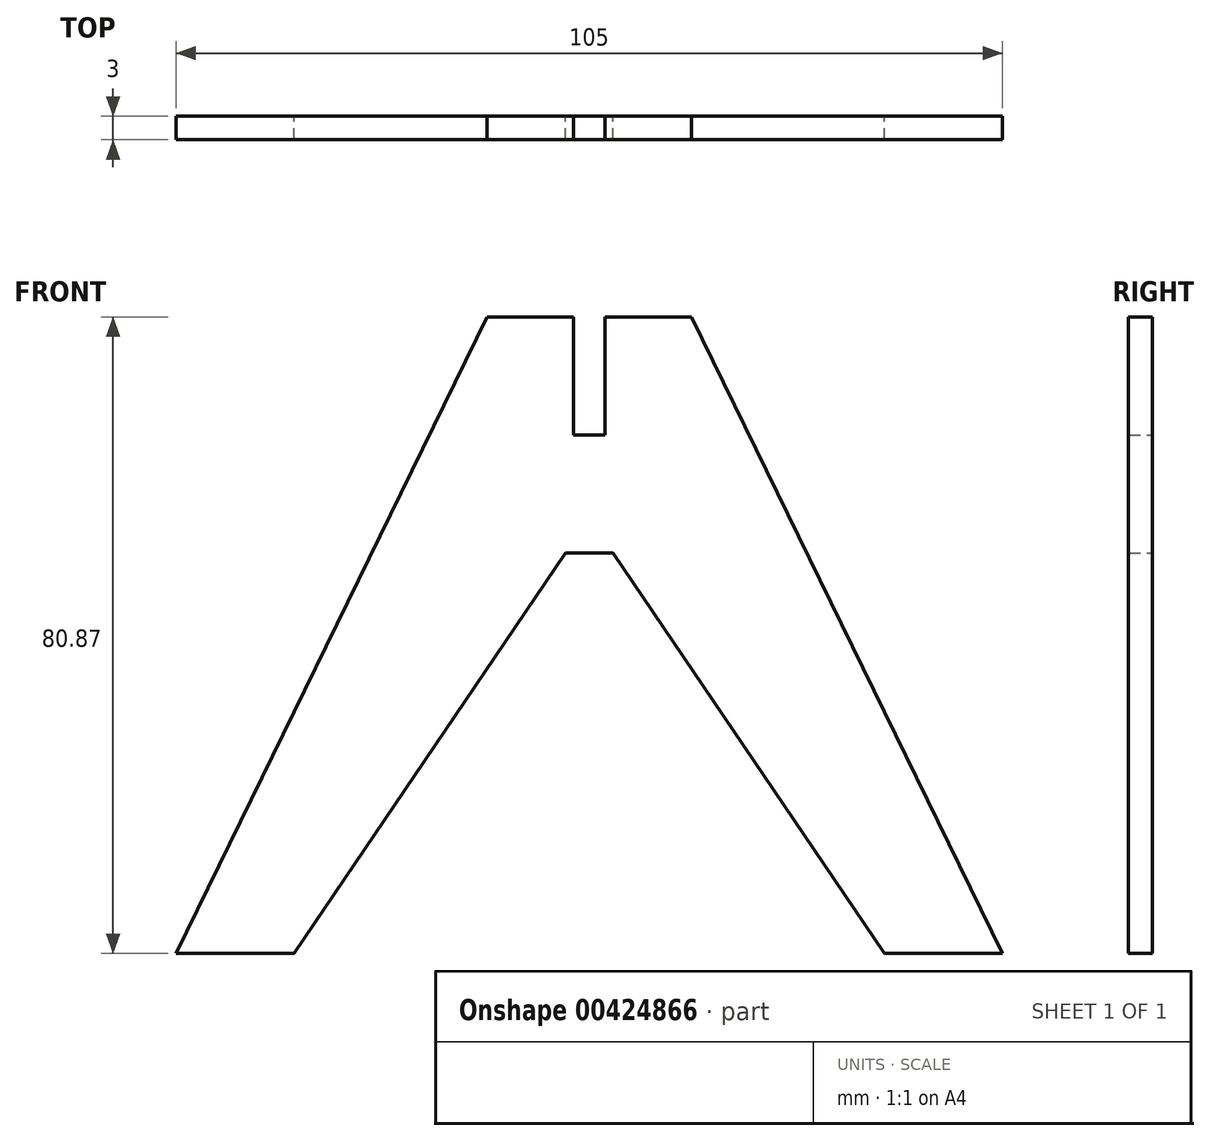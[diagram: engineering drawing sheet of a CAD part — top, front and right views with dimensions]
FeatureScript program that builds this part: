
annotation { "Feature Type Name" : "Feature", "Feature Type Description" : "" }
export const myFeature = defineFeature(function(context is Context, id is Id, definition is map)
    precondition{}
    {
        {
            var Q0;
            Q0=qCreatedBy(makeId("Front.planeOp"),FACE);
            var sketch = newSketch(context, id + "F0", { "sketchPlane" : qUnion([Q0])});
            skLineSegment(sketch, "E0", {"start": v(-77.39, -80.87) * mm, "end": v(-62.39, -80.87) * mm});
            skLineSegment(sketch, "E1", {"start": v(27.61, -80.87) * mm, "end": v(12.61, -80.87) * mm});
            skLineSegment(sketch, "E2", {"start": v(-37.89, 0) * mm, "end": v(-77.39, -80.87) * mm});
            skLineSegment(sketch, "E3", {"start": v(-11.89, 0) * mm, "end": v(27.61, -80.87) * mm});
            skPoint(sketch, "E4.orphan", {"position": v(-24.89, -80.87) * mm});
            skPoint(sketch, "E5.orphan", {"position": v(-24.89, -40.43) * mm});
            skLineSegment(sketch, "E6", {"start": v(-24.89, -30) * mm, "end": v(-27.89, -30) * mm});
            skLineSegment(sketch, "E7", {"start": v(-24.89, -30) * mm, "end": v(-21.89, -30) * mm});
            skLineSegment(sketch, "E8", {"start": v(-27.89, -30) * mm, "end": v(-62.39, -80.87) * mm});
            skLineSegment(sketch, "E9", {"start": v(-21.89, -30) * mm, "end": v(12.61, -80.87) * mm});
            skLineSegment(sketch, "E10.trimOffspring", {"start": v(12.61, -80.87) * mm, "end": v(27.61, -80.87) * mm});
            skPoint(sketch, "E11.end.orphan", {"position": v(-24.89, 0) * mm});
            skLineSegment(sketch, "E12", {"start": v(-24.89, -15) * mm, "end": v(-22.89, -15) * mm});
            skPoint(sketch, "E13.start.orphan", {"position": v(-21.89, -15) * mm});
            skLineSegment(sketch, "E14", {"start": v(-24.89, -15) * mm, "end": v(-26.89, -15) * mm});
            skPoint(sketch, "E15.start.orphan", {"position": v(-27.89, 0) * mm});
            skPoint(sketch, "E16.start.orphan", {"position": v(-21.89, 0) * mm});
            skLineSegment(sketch, "E17", {"start": v(-22.89, -15) * mm, "end": v(-22.89, 0) * mm});
            skLineSegment(sketch, "E18", {"start": v(-26.89, -15) * mm, "end": v(-26.89, 0) * mm});
            skLineSegment(sketch, "E19", {"start": v(-22.89, 0) * mm, "end": v(-11.89, 0) * mm});
            skLineSegment(sketch, "E20", {"start": v(-27.89, 0) * mm, "end": v(-37.89, 0) * mm});
            skLineSegment(sketch, "E21", {"start": v(-27.89, 0) * mm, "end": v(-26.89, 0) * mm});
            skSolve(sketch);
        }
        {
            var Q0;
            Q0 = qSketchRegion(id + "F0", true);
            extrude(context, id + "F1", {"entities" : qUnion([Q0]), "depth" : 3 * mm});
        }
    });
